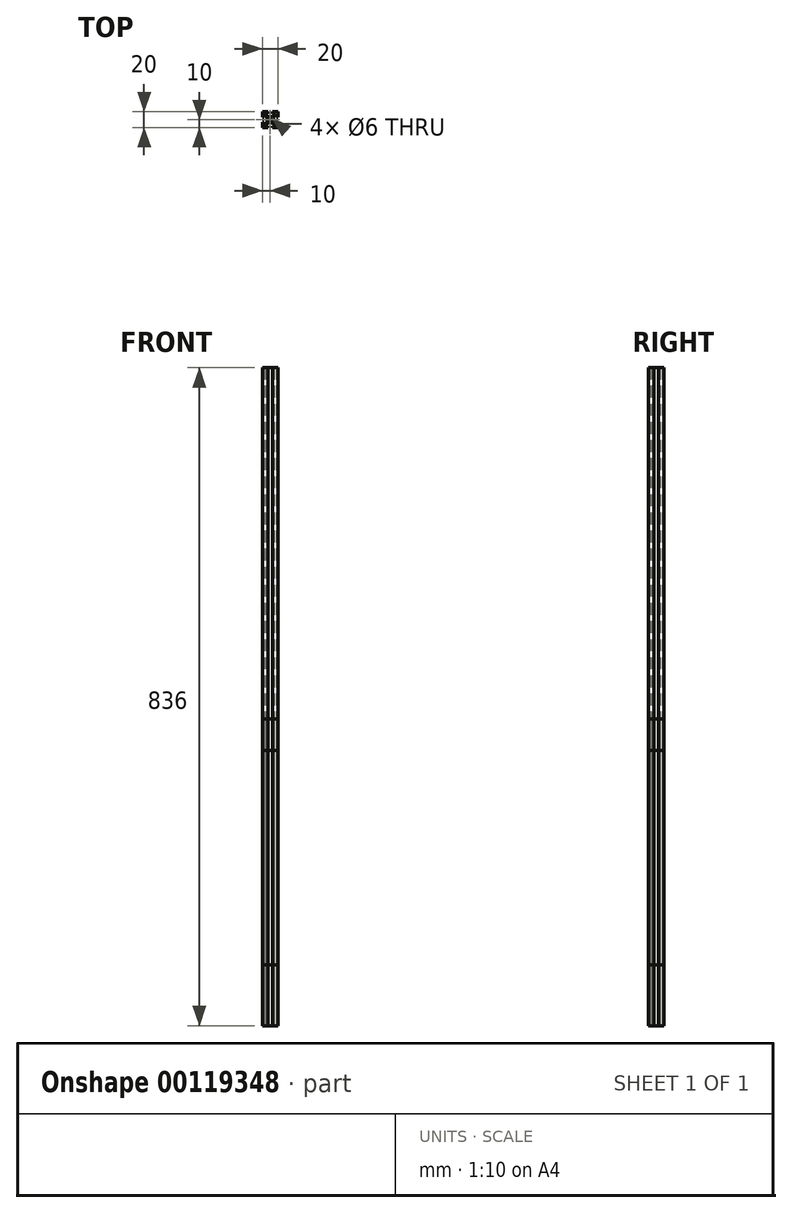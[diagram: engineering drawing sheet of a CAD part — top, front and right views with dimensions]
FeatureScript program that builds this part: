
annotation { "Feature Type Name" : "Feature", "Feature Type Description" : "" }
export const myFeature = defineFeature(function(context is Context, id is Id, definition is map)
    precondition{}
    {
        {
            var Q0;
            Q0=qCreatedBy(makeId("Top.planeOp"),FACE);
            var sketch = newSketch(context, id + "F0", { "sketchPlane" : qUnion([Q0])});
            skCircle(sketch, "E0", {"center": v(0.5, 0.3) * mm, "radius": 3 * mm});
            skLineSegment(sketch, "E1.left", {"start": v(3.5, 8.3) * mm, "end": v(3.5, 10.3) * mm});
            skLineSegment(sketch, "E2", {"start": v(3.5, 10.3) * mm, "end": v(10.5, 10.3) * mm});
            skLineSegment(sketch, "E3", {"start": v(3.5, 8.3) * mm, "end": v(5.69, 8.3) * mm});
            skLineSegment(sketch, "E4", {"start": v(0.5, 4.3) * mm, "end": v(1.71, 4.3) * mm});
            skLineSegment(sketch, "E5", {"start": v(0.5, 0.3) * mm, "end": v(10.5, 10.3) * mm, "construction": true});
            skArc(sketch, "E6", {"start": v(1.71, 4.3) * mm, "mid": v(4.53, 5.47) * mm, "end": v(5.69, 8.3) * mm});
            skLineSegment(sketch, "E7.MirrorCS", {"start": v(10.5, 3.3) * mm, "end": v(10.5, 10.3) * mm});
            skLineSegment(sketch, "E8.MirrorCS", {"start": v(8.5, 3.3) * mm, "end": v(10.5, 3.3) * mm});
            skLineSegment(sketch, "E9.MirrorCS", {"start": v(8.5, 3.3) * mm, "end": v(8.5, 5.49) * mm});
            skArc(sketch, "E10.MirrorCS", {"start": v(4.5, 1.51) * mm, "mid": v(5.67, 4.33) * mm, "end": v(8.5, 5.49) * mm});
            skLineSegment(sketch, "E11.MirrorCS", {"start": v(4.5, 0.3) * mm, "end": v(4.5, 1.51) * mm});
            skLineSegment(sketch, "E12.MirrorCS", {"start": v(-2.5, 8.3) * mm, "end": v(-2.5, 10.3) * mm});
            skLineSegment(sketch, "E13.MirrorCS", {"start": v(-2.5, 10.3) * mm, "end": v(-9.5, 10.3) * mm});
            skArc(sketch, "E14.MirrorCS", {"start": v(-3.5, 1.51) * mm, "mid": v(-4.67, 4.33) * mm, "end": v(-7.5, 5.49) * mm});
            skLineSegment(sketch, "E15.MirrorCS", {"start": v(-3.5, 0.3) * mm, "end": v(-3.5, 1.51) * mm});
            skLineSegment(sketch, "E16.MirrorCS", {"start": v(0.5, 4.3) * mm, "end": v(-0.71, 4.3) * mm});
            skLineSegment(sketch, "E17.MirrorCS", {"start": v(0.5, 0.3) * mm, "end": v(-9.5, 10.3) * mm, "construction": true});
            skLineSegment(sketch, "E18.MirrorCS", {"start": v(-7.5, 3.3) * mm, "end": v(-9.5, 3.3) * mm});
            skLineSegment(sketch, "E19.MirrorCS", {"start": v(-7.5, 3.3) * mm, "end": v(-7.5, 5.49) * mm});
            skLineSegment(sketch, "E20.MirrorCS", {"start": v(-9.5, 3.3) * mm, "end": v(-9.5, 10.3) * mm});
            skLineSegment(sketch, "E21.MirrorCS", {"start": v(-2.5, 8.3) * mm, "end": v(-4.69, 8.3) * mm});
            skArc(sketch, "E22.MirrorCS", {"start": v(-0.71, 4.3) * mm, "mid": v(-3.53, 5.47) * mm, "end": v(-4.69, 8.3) * mm});
            skLineSegment(sketch, "E23.MirrorCS", {"start": v(0.5, -3.7) * mm, "end": v(-0.71, -3.7) * mm});
            skLineSegment(sketch, "E24.MirrorCS", {"start": v(-7.5, -2.7) * mm, "end": v(-9.5, -2.7) * mm});
            skLineSegment(sketch, "E25.MirrorCS", {"start": v(-9.5, -2.7) * mm, "end": v(-9.5, -9.7) * mm});
            skArc(sketch, "E26.MirrorCS", {"start": v(-0.71, -3.7) * mm, "mid": v(-3.53, -4.87) * mm, "end": v(-4.69, -7.7) * mm});
            skLineSegment(sketch, "E27.MirrorCS", {"start": v(-2.5, -7.7) * mm, "end": v(-2.5, -9.7) * mm});
            skLineSegment(sketch, "E28.MirrorCS", {"start": v(4.5, 0.3) * mm, "end": v(4.5, -0.91) * mm});
            skArc(sketch, "E29.MirrorCS", {"start": v(4.5, -0.91) * mm, "mid": v(5.67, -3.73) * mm, "end": v(8.5, -4.89) * mm});
            skLineSegment(sketch, "E30.MirrorCS", {"start": v(8.5, -2.7) * mm, "end": v(8.5, -4.89) * mm});
            skLineSegment(sketch, "E31.MirrorCS", {"start": v(8.5, -2.7) * mm, "end": v(10.5, -2.7) * mm});
            skLineSegment(sketch, "E32.MirrorCS", {"start": v(10.5, -2.7) * mm, "end": v(10.5, -9.7) * mm});
            skArc(sketch, "E33.MirrorCS", {"start": v(1.71, -3.7) * mm, "mid": v(4.53, -4.87) * mm, "end": v(5.69, -7.7) * mm});
            skLineSegment(sketch, "E34.MirrorCS", {"start": v(0.5, 0.3) * mm, "end": v(10.5, -9.7) * mm, "construction": true});
            skLineSegment(sketch, "E35.MirrorCS", {"start": v(0.5, -3.7) * mm, "end": v(1.71, -3.7) * mm});
            skLineSegment(sketch, "E36.MirrorCS", {"start": v(3.5, -7.7) * mm, "end": v(5.69, -7.7) * mm});
            skLineSegment(sketch, "E37.MirrorCS", {"start": v(3.5, -7.7) * mm, "end": v(3.5, -9.7) * mm});
            skLineSegment(sketch, "E38.MirrorCS", {"start": v(0.5, 0.3) * mm, "end": v(-9.5, -9.7) * mm, "construction": true});
            skArc(sketch, "E39.MirrorCS", {"start": v(-3.5, -0.91) * mm, "mid": v(-4.67, -3.73) * mm, "end": v(-7.5, -4.89) * mm});
            skLineSegment(sketch, "E40.MirrorCS", {"start": v(-2.5, -9.7) * mm, "end": v(-9.5, -9.7) * mm});
            skLineSegment(sketch, "E41.MirrorCS", {"start": v(3.5, -9.7) * mm, "end": v(10.5, -9.7) * mm});
            skLineSegment(sketch, "E42.MirrorCS", {"start": v(-2.5, -7.7) * mm, "end": v(-4.69, -7.7) * mm});
            skLineSegment(sketch, "E43.MirrorCS", {"start": v(-3.5, 0.3) * mm, "end": v(-3.5, -0.91) * mm});
            skLineSegment(sketch, "E44.MirrorCS", {"start": v(-7.5, -2.7) * mm, "end": v(-7.5, -4.89) * mm});
            skSolve(sketch);
        }
        {
            var Q0;
            Q0=makeQuery(id+"F0.imprint","IMPRINT",FACE,{"disambiguationData":[TD([[makeQuery(id+"F0.imprint","IMPRINT",EDGE,{"derivedFrom":sQuery(id+"F0.wireOp",EDGE,"E0")}),-1.0]])]});
            var Q1;
            Q1=sQuery(id+"F0.wireOp",EDGE,"E0");
            var Q2;
            Q2=sQuery(id+"F0.wireOp",EDGE,"E1.left");
            var Q3;
            Q3=sQuery(id+"F0.wireOp",EDGE,"E2");
            var Q4;
            Q4=sQuery(id+"F0.wireOp",EDGE,"E3");
            var Q5;
            Q5=sQuery(id+"F0.wireOp",EDGE,"E4");
            var Q6;
            Q6=sQuery(id+"F0.wireOp",EDGE,"E6");
            var Q7;
            Q7=sQuery(id+"F0.wireOp",EDGE,"E7.MirrorCS");
            var Q8;
            Q8=sQuery(id+"F0.wireOp",EDGE,"E8.MirrorCS");
            var Q9;
            Q9=sQuery(id+"F0.wireOp",EDGE,"E9.MirrorCS");
            var Q10;
            Q10=sQuery(id+"F0.wireOp",EDGE,"E10.MirrorCS");
            var Q11;
            Q11=sQuery(id+"F0.wireOp",EDGE,"E11.MirrorCS");
            var Q12;
            Q12=sQuery(id+"F0.wireOp",EDGE,"E12.MirrorCS");
            var Q13;
            Q13=sQuery(id+"F0.wireOp",EDGE,"E13.MirrorCS");
            var Q14;
            Q14=sQuery(id+"F0.wireOp",EDGE,"E14.MirrorCS");
            var Q15;
            Q15=sQuery(id+"F0.wireOp",EDGE,"E15.MirrorCS");
            var Q16;
            Q16=sQuery(id+"F0.wireOp",EDGE,"E16.MirrorCS");
            var Q17;
            Q17=sQuery(id+"F0.wireOp",EDGE,"E18.MirrorCS");
            var Q18;
            Q18=sQuery(id+"F0.wireOp",EDGE,"E19.MirrorCS");
            var Q19;
            Q19=sQuery(id+"F0.wireOp",EDGE,"E20.MirrorCS");
            var Q20;
            Q20=sQuery(id+"F0.wireOp",EDGE,"E21.MirrorCS");
            var Q21;
            Q21=sQuery(id+"F0.wireOp",EDGE,"E22.MirrorCS");
            var Q22;
            Q22=sQuery(id+"F0.wireOp",EDGE,"E23.MirrorCS");
            var Q23;
            Q23=sQuery(id+"F0.wireOp",EDGE,"E24.MirrorCS");
            var Q24;
            Q24=sQuery(id+"F0.wireOp",EDGE,"E25.MirrorCS");
            var Q25;
            Q25=sQuery(id+"F0.wireOp",EDGE,"E26.MirrorCS");
            var Q26;
            Q26=sQuery(id+"F0.wireOp",EDGE,"E27.MirrorCS");
            var Q27;
            Q27=sQuery(id+"F0.wireOp",EDGE,"E28.MirrorCS");
            var Q28;
            Q28=sQuery(id+"F0.wireOp",EDGE,"E29.MirrorCS");
            var Q29;
            Q29=sQuery(id+"F0.wireOp",EDGE,"E30.MirrorCS");
            var Q30;
            Q30=sQuery(id+"F0.wireOp",EDGE,"E31.MirrorCS");
            var Q31;
            Q31=sQuery(id+"F0.wireOp",EDGE,"E32.MirrorCS");
            var Q32;
            Q32=sQuery(id+"F0.wireOp",EDGE,"E33.MirrorCS");
            var Q33;
            Q33=sQuery(id+"F0.wireOp",EDGE,"E35.MirrorCS");
            var Q34;
            Q34=sQuery(id+"F0.wireOp",EDGE,"E36.MirrorCS");
            var Q35;
            Q35=sQuery(id+"F0.wireOp",EDGE,"E37.MirrorCS");
            var Q36;
            Q36=sQuery(id+"F0.wireOp",EDGE,"E39.MirrorCS");
            var Q37;
            Q37=sQuery(id+"F0.wireOp",EDGE,"E40.MirrorCS");
            var Q38;
            Q38=sQuery(id+"F0.wireOp",EDGE,"E41.MirrorCS");
            var Q39;
            Q39=sQuery(id+"F0.wireOp",EDGE,"E42.MirrorCS");
            var Q40;
            Q40=sQuery(id+"F0.wireOp",EDGE,"E43.MirrorCS");
            var Q41;
            Q41=sQuery(id+"F0.wireOp",EDGE,"E44.MirrorCS");
            extrude(context, id + "F1", {"entities" : qUnion([Q0]), "surfaceEntities" : qUnion([Q1, Q2, Q3, Q4, Q5, Q6, Q7, Q8, Q9, Q10, Q11, Q12, Q13, Q14, Q15, Q16, Q17, Q18, Q19, Q20, Q21, Q22, Q23, Q24, Q25, Q26, Q27, Q28, Q29, Q30, Q31, Q32, Q33, Q34, Q35, Q36, Q37, Q38, Q39, Q40, Q41]), "depth" : 350 * mm});
        }
        {
            var Q0;
            Q0 = qSketchRegion(id + "F0", true);
            extrude(context, id + "F2", {"entities" : qUnion([Q0]), "depth" : 77.2 * mm});
        }
        {
            var Q0;
            Q0 = qSketchRegion(id + "F0", true);
            extrude(context, id + "F3", {"entities" : qUnion([Q0]), "depth" : 390 * mm});
        }
        {
            var Q0;
            Q0 = qSketchRegion(id + "F0", true);
            extrude(context, id + "F4", {"entities" : qUnion([Q0]), "depth" : 836 * mm});
        }
    });
